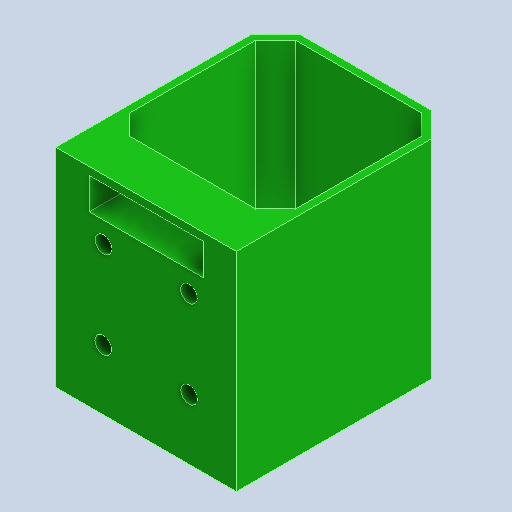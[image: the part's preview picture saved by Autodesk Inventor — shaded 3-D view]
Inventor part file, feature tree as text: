
AUTODESK INVENTOR PART (.ipt)
format: ipt  version: 2023 (Build 270158000, 158)  size: 425,472 bytes
history: native  units: mm
features: other x21, sketch x8, extrude x7, projected_geometry x4, loft x2
ambient origin geometry x8: Origin, YZ Plane, XZ Plane, XY Plane, X Axis, Y Axis, Z Axis, Center Point
bodies: Solide1 (feature_tree)
feature tree (42):
  sketch  "Esquisse1"
  other  "Plan de construction1"
  extrude  "Extrusion1"  Depth=200.0mm
  other  "Plan de construction5"
  extrude  "Extrusion14"  Depth=220.0mm
  sketch  "Esquisse20"
  other  "Plan de construction6"
  extrude  "Extrusion15"  Depth=2.0mm
  extrude  "Extrusion16"  Depth=2.0mm
  sketch  "Esquisse21"
  other  "Plan de construction7"
  extrude  "Extrusion17"  Depth=5.0mm TaperAngle=0.0deg
  loft  "Lissage2"
  loft  "Lissage3"
  sketch  "Esquisse22"
  sketch  "Esquisse24"
  extrude  "Extrusion20"  Depth=2.0mm
  extrude  "Extrusion21"  Depth=3.0mm TaperAngle=0.0deg
  sketch  "Esquisse2"
  other  "Référence1"
  sketch  "Esquisse19"
  other  "Référence3"
  other  "Référence4"
  other  "Référence5"
  other  "Référence6"
  other  "Référence7"
  other  "Référence8"
  other  "Référence9"
  other  "Référence10"
  projected_geometry  "Boucle projetée10"
  other  "Référence11"
  projected_geometry  "Boucle projetée11"
  projected_geometry  "Boucle projetée12"
  projected_geometry  "Boucle projetée13"
  other  "Arêtes3"
  other  "Arêtes4"
  other  "Arêtes5"
  other  "Arêtes6"
  sketch  "Esquisse25"
  other  "<userpath>\Desktop\Robot\Robotbebou.iam"
  other  "Robotbebou.iam"
  other  "SF2423-10B41_MIR1:1"
